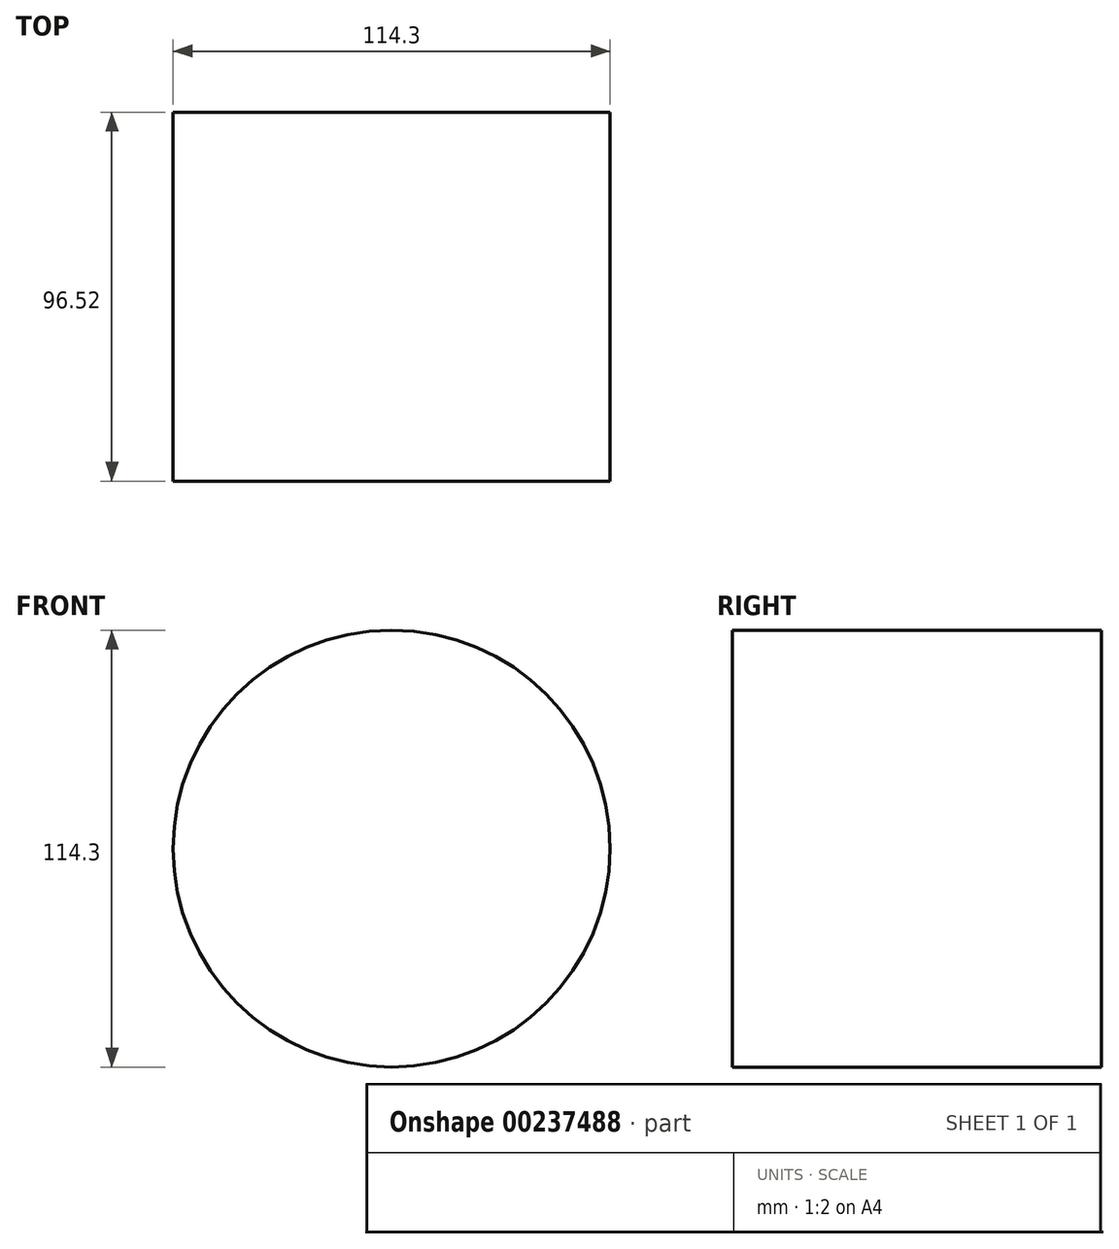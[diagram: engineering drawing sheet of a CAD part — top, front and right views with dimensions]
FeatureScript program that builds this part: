
annotation { "Feature Type Name" : "Feature", "Feature Type Description" : "" }
export const myFeature = defineFeature(function(context is Context, id is Id, definition is map)
    precondition{}
    {
        {
            var Q0;
            Q0=qCreatedBy(makeId("Front.planeOp"),FACE);
            var sketch = newSketch(context, id + "F0", { "sketchPlane" : qUnion([Q0])});
            skCircle(sketch, "E0", {"center": v(0, 0) * mm, "radius": 57.15 * mm});
            skSolve(sketch);
        }
        {
            var Q0;
            Q0 = qSketchRegion(id + "F0", true);
            extrude(context, id + "F1", {"entities" : qUnion([Q0]), "depth" : 96.52 * mm});
        }
    });
